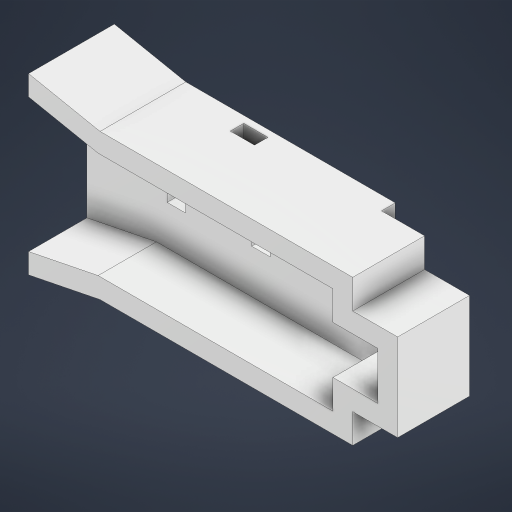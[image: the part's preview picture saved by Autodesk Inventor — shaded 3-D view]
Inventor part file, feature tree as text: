
AUTODESK INVENTOR PART (.ipt)
format: ipt  version: 2024.1 (Build 281209000, 209)  size: 4,432,384 bytes
history: native  units: mm
features: extrude x8, sketch x8, projected_geometry x7, plane x3, other x2
ambient origin geometry x8: Origin, YZ Plane, XZ Plane, XY Plane, X Axis, Y Axis, Z Axis, Center Point
bodies: Solid1 (feature_tree)
feature tree (28):
  other  "3D_PCB1_2024-08-12"
  plane  "Work Plane1"
  extrude  "Extrusion1"  Depth=14.696mm
  sketch  "Sketch3"  dims[d2=10.0mm d3=10.0mm]
  plane  "Work Plane2"
  extrude  "Extrusion2"  Depth=10.0mm
  extrude  "Extrusion3"  Depth=3.0mm
  extrude  "Extrusion4"  Depth=3.0mm
  extrude  "Extrusion5"  Depth=2.76mm TaperAngle=0.0deg
  plane  "Work Plane3"
  extrude  "Extrusion6"  Depth=13.0mm
  extrude  "Extrusion7"  Depth=14.939mm
  extrude  "Extrusion8"  Depth=6.0mm
  sketch  "Sketch2"  dims[d0=4.1mm d1=14.696mm]
  sketch  "Sketch4"  dims[d4=10.0mm d5=3.0mm]
  sketch  "Sketch5"  dims[d6=3.0mm d7=3.0mm]
  sketch  "Sketch6"  dims[d8=0.0mm d9=2.76mm d10=0.0mm]
  projected_geometry  "Projected Loop1"
  projected_geometry  "Projected Loop2"
  sketch  "Sketch7"  dims[d11=0.0mm d12=3.328mm d13=0.0mm d14=13.0mm]
  sketch  "Sketch8"  dims[d15=47.5mm d16=14.939mm]
  projected_geometry  "Projected Loop3"
  sketch  "Sketch10"  dims[d17=3.0mm d18=5.0mm d19=10.0mm d20=10.0mm d21=5.0mm d22=0.3mm d23=5.0mm d24=0.3mm d25=13.0mm d26=0.0mm d28=3.0mm d29=0.0mm d30=0.0mm d31=0.0mm d32=5.4mm d33=3.0mm d34=0.0mm d35=3.0mm d36=0.0mm d45=6.0mm d46=0.0mm d47=0.0mm]
  projected_geometry  "Projected Loop4"
  other  "3D_PCB1_2024-08-12.obj"
  projected_geometry  "Project Cut Edges1"
  projected_geometry  "Project Cut Edges2"
  projected_geometry  "Project Cut Edges3"
